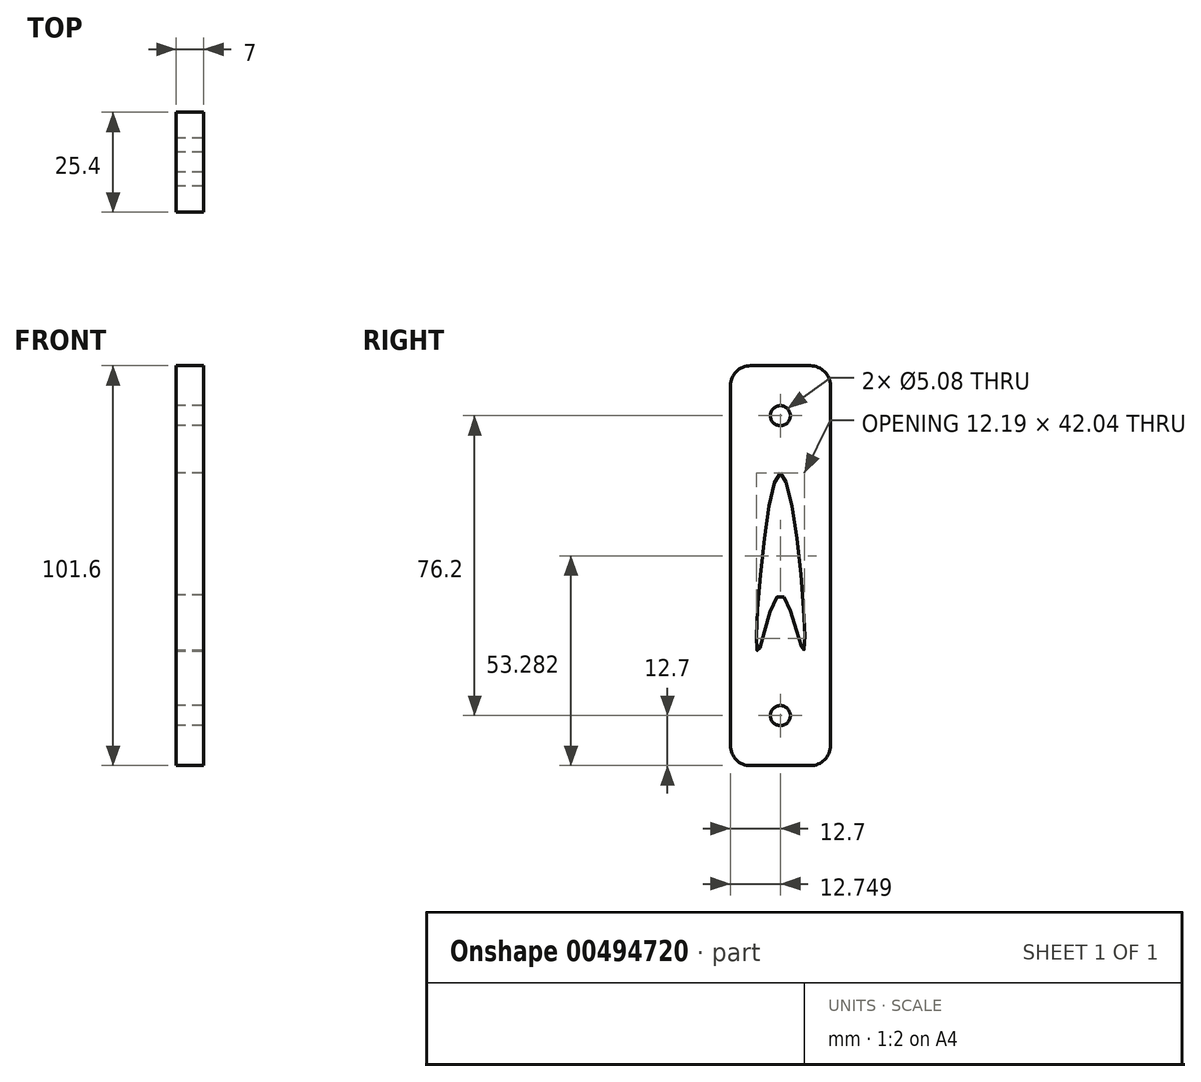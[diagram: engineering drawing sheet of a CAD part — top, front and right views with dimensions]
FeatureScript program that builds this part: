
annotation { "Feature Type Name" : "Feature", "Feature Type Description" : "" }
export const myFeature = defineFeature(function(context is Context, id is Id, definition is map)
    precondition{}
    {
        {
            var Q0;
            Q0=qCreatedBy(makeId("Front.planeOp"),FACE);
            var sketch = newSketch(context, id + "F0", { "sketchPlane" : qUnion([Q0])});
            skLineSegment(sketch, "E0.bottom", {"start": v(0, 101.6) * mm, "end": v(7, 101.6) * mm});
            skLineSegment(sketch, "E0.top", {"start": v(0, 0) * mm, "end": v(7, 0) * mm});
            skLineSegment(sketch, "E0.left", {"start": v(0, 101.6) * mm, "end": v(0, 0) * mm});
            skLineSegment(sketch, "E0.right", {"start": v(7, 101.6) * mm, "end": v(7, 0) * mm});
            skLineSegment(sketch, "E1", {"start": v(7, 0) * mm, "end": v(7, 3.65) * mm});
            skSolve(sketch);
        }
        {
            var Q0;
            Q0=qSketchRegion(id+"F0",true);
            extrude(context, id + "F1", {"entities" : qUnion([Q0]), "depth" : 25.4 * mm});
        }
        {
            var Q0;
            Q0=qCreatedBy(makeId("Right.planeOp"),FACE);
            var sketch = newSketch(context, id + "F2", { "sketchPlane" : qUnion([Q0])});
            skCircle(sketch, "E2", {"center": v(-12.7, 88.9) * mm, "radius": 2.43 * mm});
            skFitSpline(sketch, "E3", {"points": [v(-12.7, 74.3) * mm, v(-6.83, 29.21) * mm, v(-12.7, 43.42) * mm, v(-18.49, 28.95) * mm, v(-12.7, 74.3) * mm]});
            skPoint(sketch, "E4", {"position": v(-12.7, 12.7) * mm});
            skSolve(sketch);
        }
        {
            var Q0;
            Q0=sQuery(id+"F2.wireOp",VERTEX,"E2.center");
            var Q1;
            Q1=makeQuery(id+"F1.opExtrude","SWEPT_BODY",BODY,{"disambiguationData":[OSD([sQuery(id+"F0.wireOp",EDGE,"E0.bottom"),sQuery(id+"F0.wireOp",EDGE,"E0.top"),sQuery(id+"F0.wireOp",EDGE,"E0.left"),sQuery(id+"F0.wireOp",EDGE,"E0.right"),sQuery(id+"F0.wireOp",EDGE,"E1")])]});
            hole(context, id + "F3", {"style" : HoleStyle.SIMPLE, "endStyle" : HoleEndStyle.THROUGH, "oppositeDirection" : true, "holeDiameter" : 5.08 * mm, "isTappedThrough" : true, "tappedDepth" : 12.7 * mm, "tapClearance" : 3, "locations" : qUnion([Q0]), "scope" : qUnion([Q1])});
        }
        {
            var Q0;
            Q0=qSketchRegion(id+"F2",true);
            extrude(context, id + "F4", {"entities" : qUnion([Q0]), "operationType" : NewBodyOperationType.REMOVE, "endBound" : BoundingType.THROUGH_ALL, "depth" : 25.4 * mm});
        }
        {
            var Q0;
            Q0=sQuery(id+"F2.wireOp",VERTEX,"E4");
            var Q1;
            Q1=makeQuery(id+"F1.opExtrude","SWEPT_BODY",BODY,{"disambiguationData":[OSD([sQuery(id+"F0.wireOp",EDGE,"E0.bottom"),sQuery(id+"F0.wireOp",EDGE,"E0.top"),sQuery(id+"F0.wireOp",EDGE,"E0.left"),sQuery(id+"F0.wireOp",EDGE,"E0.right"),sQuery(id+"F0.wireOp",EDGE,"E1")])]});
            hole(context, id + "F5", {"style" : HoleStyle.SIMPLE, "endStyle" : HoleEndStyle.THROUGH, "oppositeDirection" : true, "holeDiameter" : 5.08 * mm, "isTappedThrough" : true, "tappedDepth" : 12.7 * mm, "tapClearance" : 3, "locations" : qUnion([Q0]), "scope" : qUnion([Q1])});
        }
        {
            var Q0;
            Q0=makeQuery(id+"F1.opExtrude","CAP_EDGE",EDGE,{"disambiguationData":[OSD([sQuery(id+"F0.wireOp",EDGE,"E0.bottom")])],"isStart":false});
            var Q1;
            Q1=makeQuery(id+"F1.opExtrude","CAP_EDGE",EDGE,{"disambiguationData":[OSD([sQuery(id+"F0.wireOp",EDGE,"E0.bottom")])],"isStart":true});
            fillet(context, id + "F6", {"entities" : qUnion([Q0, Q1]), "radius" : 5.08 * mm, "tangentPropagation" : true, "allowEdgeOverflow" : false});
        }
        {
            var Q0;
            Q0=makeQuery(id+"F1.opExtrude","CAP_EDGE",EDGE,{"disambiguationData":[OSD([sQuery(id+"F0.wireOp",EDGE,"E0.top")])],"isStart":false});
            var Q1;
            Q1=makeQuery(id+"F1.opExtrude","CAP_EDGE",EDGE,{"disambiguationData":[OSD([sQuery(id+"F0.wireOp",EDGE,"E0.top")])],"isStart":true});
            fillet(context, id + "F7", {"entities" : qUnion([Q0, Q1]), "radius" : 5.08 * mm, "tangentPropagation" : true, "allowEdgeOverflow" : false});
        }
    });
